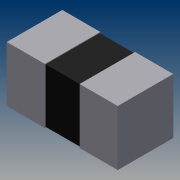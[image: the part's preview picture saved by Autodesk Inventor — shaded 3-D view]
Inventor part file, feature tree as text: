
AUTODESK INVENTOR PART (.ipt)
format: ipt  version: 2011 (Build 150239000, 239)  size: 112,128 bytes
history: native  units: mm
features: extrude x5, sketch x5, other x1
ambient origin geometry x8: Origin, YZ Plane, XZ Plane, XY Plane, X Axis, Y Axis, Z Axis, Center Point
feature tree (11):
  other  "Твердое тело1"
  extrude  "Выдавливание1"  Depth=1.6mm
  extrude  "Выдавливание2"  Depth=0.8mm
  extrude  "Выдавливание3"  Depth=0.8mm
  extrude  "Выдавливание4"  Depth=0.8mm
  extrude  "Выдавливание5"  Depth=0.4mm
  sketch  "Эскиз1"
  sketch  "Эскиз2"
  sketch  "Эскиз3"
  sketch  "Эскиз4"
  sketch  "Эскиз5"
